SOLIDWORKS PART (.sldprt)
format: sldprt  version: not decoded by parser v0  size: 743,424 bytes
history: native  units: mm
features: sketch x17, plane x15, cut_revolve x2, extrude x2, material x1, cut_extrude x1, shell x1 + 1 further entry (+9 scaffold rows collapsed)
feature tree (49):
  "Annotations"  RD1=15.75deg
  scaffold x9  (default folders/planes/origin — collapsed)
  material  "Matériau <non spécifié>"
  plane  "Plan de face"
  plane  "Plan de dessus"
  plane  "Plan de droite"
  sketch  "Esquisse1"  dims[c1.D1=625.0mm c1.D2=460.0mm c1.D3=545.0mm c1.D4=27.0mm c1.D5=500.0mm c1.D6=445.0mm c1.D7=670.0mm c2.D1=622.0mm c2.D2=670.0mm c2.D3=545.0mm c2.D4=460.0mm c2.D5=445.0mm c2.D6=495.0mm c2.D7=535.0mm c2.D8=27.0mm c2.D9=8.0mm c2.D10=155.0mm c2.D11=400.0mm c2.D12=~545.374305mm c3.D12=56.0deg]
  plane  "Plan1"
  plane  "Plan2"
  sketch  "Esquisse2"  dims[c1.D2=75.0mm c1.D1=102.0mm c1.D3=103.0mm c2.D1=102.0mm c2.D4=~138.45102mm c3.D4=45.0deg]
  sketch  "Esquisse3"  dims[D1=112.0mm]
  plane  "Plan3"
  sketch  "Esquisse4"  dims[D1=500.0mm]
  plane  "Plan4"
  plane  "Plan5"
  plane  "Plan6"
  plane  "Plan7"
  plane  "Plan8"
  plane  "Plan10"
  sketch  "Esquisse5"  dims[D1=16.0mm D2=27.0mm]
  sketch  "Esquisse6"  dims[D1=30.0mm D2=18.5mm]
  sketch  "Esquisse7"  dims[D1=40.0mm D2=18.0mm]
  sketch  "Esquisse8"  dims[D1=40.0mm D2=20.0mm]
  sketch  "Esquisse9"  dims[D1=38.5mm D2=25.0mm]
  sketch  "Esquisse10"  dims[D1=28.0mm D2=36.0mm]
  sketch  "Esquisse11"  dims[D1=0.0mm]
  sketch  "Esquisse13"  dims[D6=40.0mm D1=40.0mm D2=50.0mm D3=5.0mm D4=116.0mm D5=35.0mm]
  cut_revolve  "Enlèvement de matière-Révolution2"  Angle=360deg
  sketch  "Esquisse14"  dims[D1=15.0mm]
  cut_extrude  "Enlèv. mat.-Extru.1"  [1 undecoded]
  sketch  "Esquisse20"  dims[c1.D1=32.0mm c1.D6=30.0mm c1.D2=60.0mm c1.D3=57.0mm c1.D4=22.0mm c2.D2=82.5mm c2.D5=50.0mm c2.D7=20.0mm c2.D8=25.0mm c3.D7=22.0mm]
  cut_revolve  "Enlèvement de matière-Révolution3"  Angle=360deg
  shell  "Coque4"  Thickness=2mm
  plane  "Plan11"  Offset=50mm
  sketch  "Esquisse16"  dims[c1.D1=27.0mm c1.D2=12.0mm c1.D5=2.5mm c1.D6=10.0mm c1.D8=4.2mm c1.D3=23.0mm c1.D4=7.0mm c2.D6=10.0mm c2.D7=~44.215091mm c3.D7=11.5deg]
  extrude  "Extrusion2"  Depth=7mm
  sketch  "Esquisse21"
  extrude  "Extrusion3"  Depth=8mm
  plane  "Plan12"  Offset=39.5mm
  sketch  "Esquisse22"  dims[D2=5.0mm D1=285.0mm]
  plane  "Plan13"  Offset=65mm
decode coverage: 21 of 23 modeling features carry decoded parameters; 1 rows unclassified (native names shown)
note: ~ marks probable driven/reference dimensions
note: 1 parameter value undecoded
note: suppression state not decoded; provenance and decode notes live in map.json
